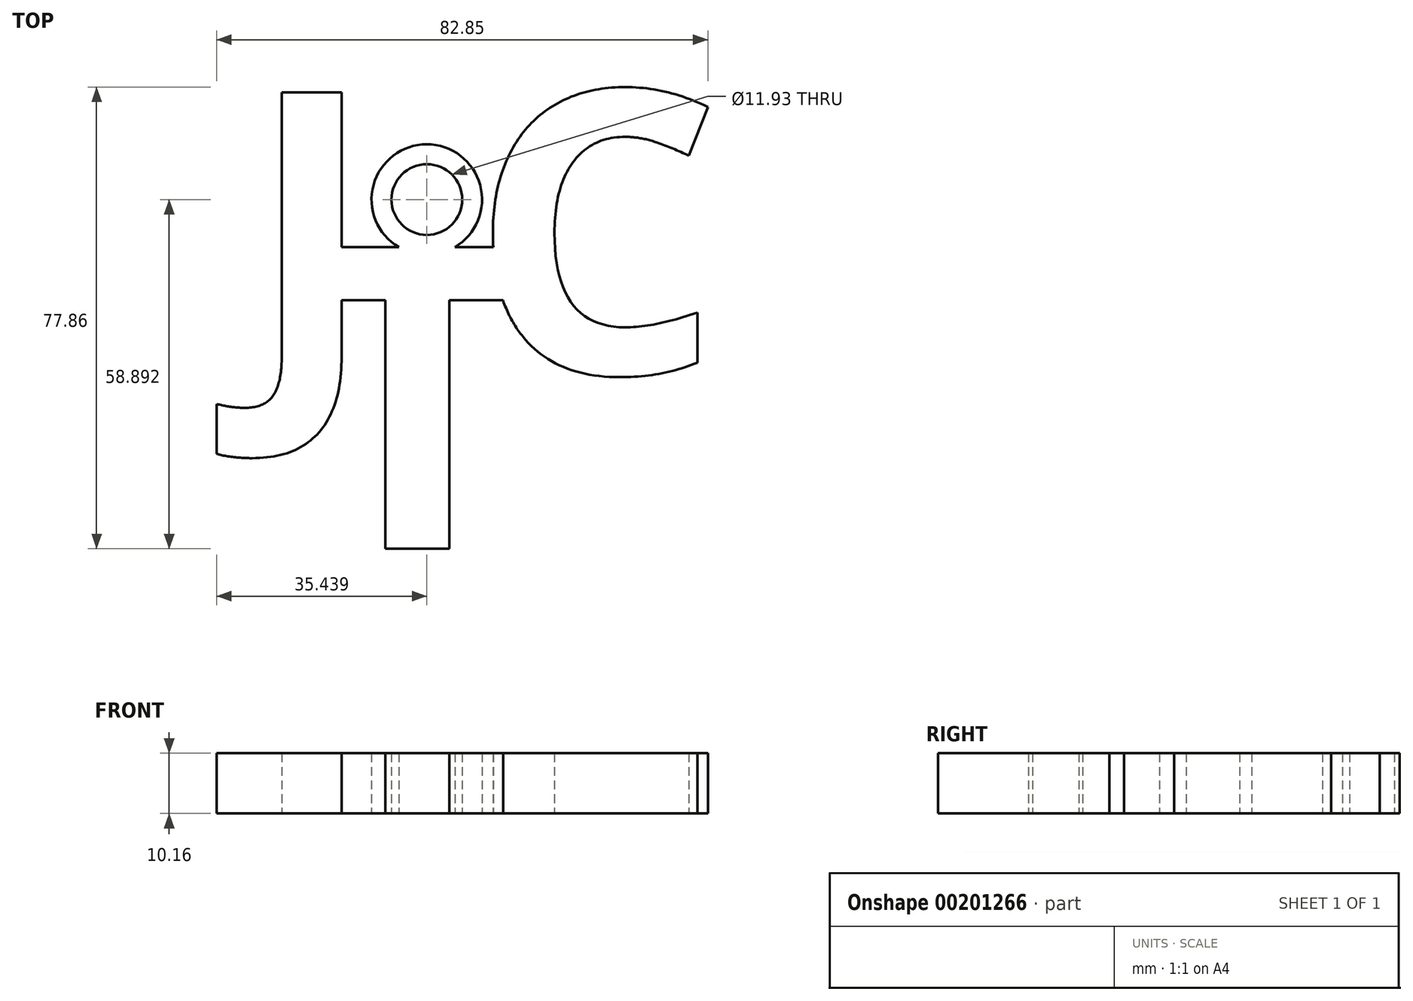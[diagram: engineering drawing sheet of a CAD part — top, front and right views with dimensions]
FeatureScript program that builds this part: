
annotation { "Feature Type Name" : "Feature", "Feature Type Description" : "" }
export const myFeature = defineFeature(function(context is Context, id is Id, definition is map)
    precondition{}
    {
        {
            var Q0;
            Q0=qCreatedBy(makeId("Top.planeOp"),FACE);
            var sketch = newSketch(context, id + "F0", { "sketchPlane" : qUnion([Q0])});
            skText(sketch, "E0", { "text": "J", "fontName": "OpenSans-Bold.ttf"});
            skText(sketch, "E1", { "text": "T", "fontName": "OpenSans-Bold.ttf"});
            skText(sketch, "E2", { "text": "C", "fontName": "OpenSans-Bold.ttf"});
            skCircle(sketch, "E3", {"center": v(-105.07, 45.7) * mm, "radius": 9.32 * mm});
            skCircle(sketch, "E4", {"center": v(-105.07, 45.7) * mm, "radius": 5.97 * mm});
            const initialGuessF0  = {"E0": [-0.13555, 0.0161, 1, 0, 0.04809], "E1": [-0.1273, -0.0132, 1, 0, 0.0513], "E2": [-0.0978, 0.01639, 1, 0, 0.048]};
            skSetInitialGuess(sketch, initialGuessF0);
            skSolve(sketch);
        }
        {
            var Q0;
            Q0 = qSketchRegion(id + "F0", true);
            extrude(context, id + "F1", {"entities" : qUnion([Q0]), "depth" : 10.16 * mm});
        }
    });
